# Revit family: NAU_Naughtone_Stng_Polly_StarBase
name_source: partatom
category: Furniture
revit_build: Autodesk Revit 2015 (Build: 20140903_1530(x64)
units: mm (PartAtom-declared; Revit-internal decimal feet)

## types (4) — shared parameters
AssetType = Movable
BIMObjectName = NAU_Naughtone_Seating_Polly_StarBase
CodePerformance = Pr_40_50_12 : Chairs, seats and benches
Color = Various
DurationUnit = year
Finish = Polypropylene
IfcExportAs = IfcFurnishingElementType
IfcExportType = CHAIR
Keynote = Pr_40_50_12
MainColor = Various
ManufacturerAddress = Knaresborough Tech Park, Manse Lane, Knaresborough, HG5 8LF
ManufacturerName = Naughtone
ManufacturerURL = www.naughtone.com
Material = Steel/plastic
NBSDescription = Seating
NBSReference = 45-35-72/352
Name = Seating_Polly_StarBase_Naughtone
NominalHeight = 785 mm
NominalLength = 530 mm
ProductInformation = www.naughtone.com/products/polly/
Revision = 1
Shape = Rectangular
SustainabilityPerformance = FSC certified. FISP certified. ISO 14001
URL = www.naughtone.com
Uniclass2015Code = Pr_40_50_12
Uniclass2015Title = Chairs, seats and benches
Uniclass2015Version = Products v1.10
Version = 1
WarrantyDescription = Request warranty information from naughtone
WarrantyDurationLabor = 5
WarrantyDurationParts = 5
WarrantyDurationUnit = year

## per-type parameters (varying)
| type | Description | Has4StarBase | Has5StarBase | IsArmchair | ModelReference | NominalWidth | Size |
| POLLYCH4S | Polly 4 Star Base | Yes | No | No | Polly 4 Star Base | 500 mm | 530 x 500 x 785mm |
| POLLYACH4S | Polly Armchair 4 Star Base | Yes | No | Yes | Polly Armchair 4 Star Base | 635 mm | 530 x 500 x 785mm |
| POLLYCH5S | Polly 5 Star Base | No | Yes | No | Polly 5 Star Base | 500 mm | 530 x 500 x 785mm |
| POLLYACH5S | Polly Armchair 5 Star Base | No | Yes | Yes | Polly Armchair 5 Star Base | 635 mm | 530 x 635 x 785mm |

note: column(s) folded — value = type name in every type: Model, ModelNumber

## geometry (parser evidence)
native form markers: Sweep x2
no freeform markers — native parametric forms only
